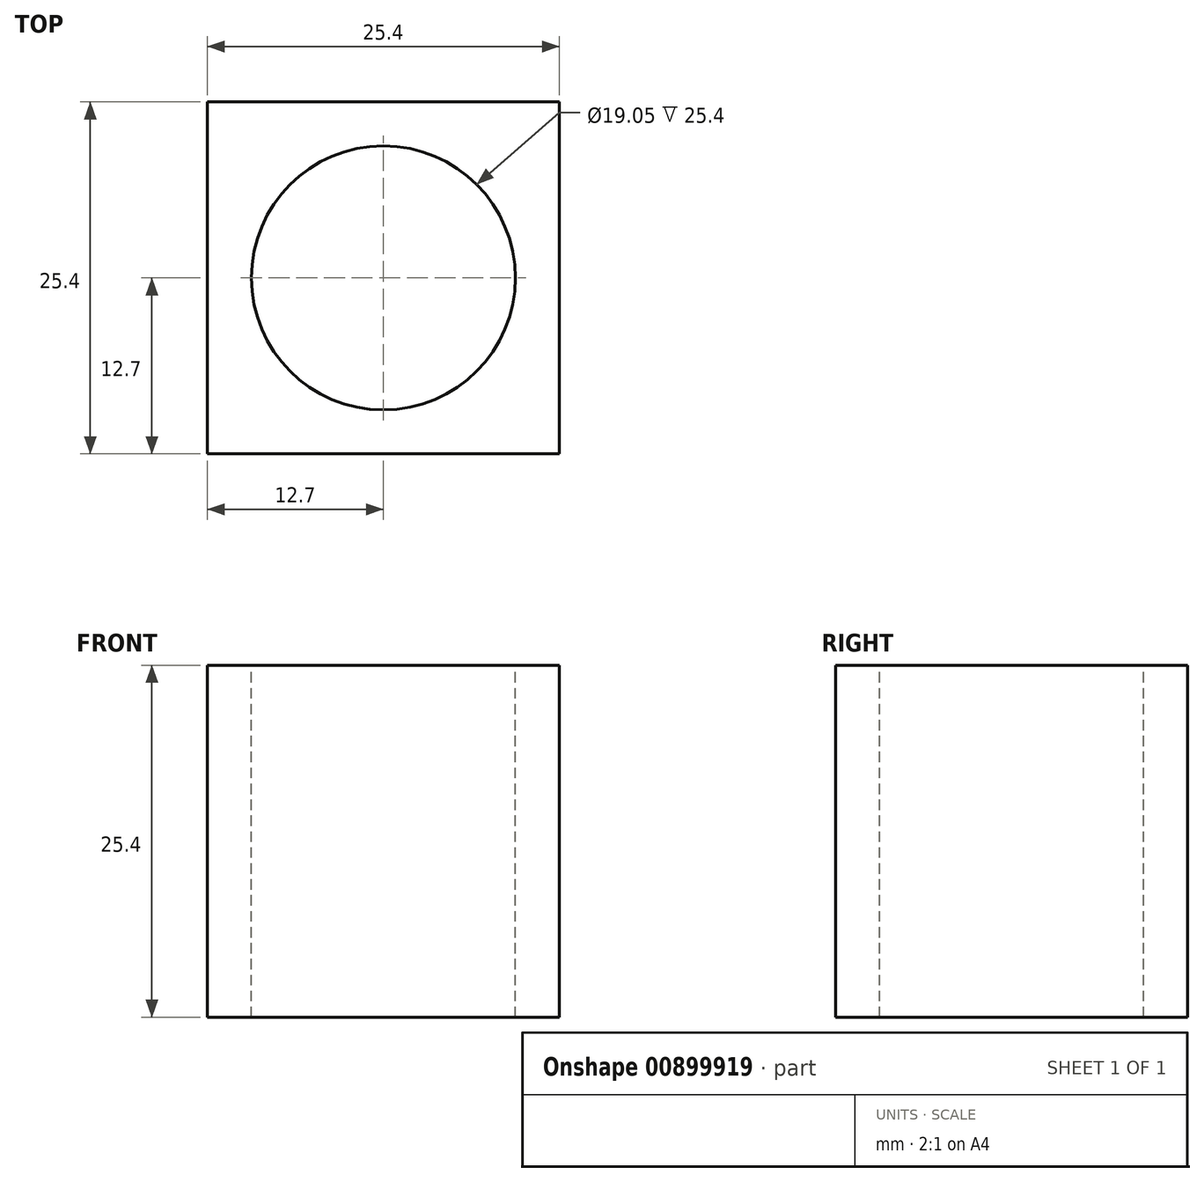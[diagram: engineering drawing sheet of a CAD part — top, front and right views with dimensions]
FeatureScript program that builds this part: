
annotation { "Feature Type Name" : "Feature", "Feature Type Description" : "" }
export const myFeature = defineFeature(function(context is Context, id is Id, definition is map)
    precondition{}
    {
        {
            var Q0;
            Q0=qCreatedBy(makeId("Top.planeOp"),FACE);
            var sketch = newSketch(context, id + "F0", { "sketchPlane" : qUnion([Q0])});
            skLineSegment(sketch, "E0.bottom", {"start": v(12.7, -12.7) * mm, "end": v(-12.7, -12.7) * mm});
            skLineSegment(sketch, "E0.top", {"start": v(12.7, 12.7) * mm, "end": v(-12.7, 12.7) * mm});
            skLineSegment(sketch, "E0.left", {"start": v(12.7, -12.7) * mm, "end": v(12.7, 12.7) * mm});
            skLineSegment(sketch, "E0.right", {"start": v(-12.7, -12.7) * mm, "end": v(-12.7, 12.7) * mm});
            skPoint(sketch, "E0.middle", {"position": v(0, 0) * mm});
            skSolve(sketch);
        }
        {
            var Q0;
            Q0=qSketchRegion(id+"F0",true);
            extrude(context, id + "F1", {"entities" : qUnion([Q0]), "depth" : 25.4 * mm, "offsetDistance" : 25.4 * mm});
        }
        {
            var Q0;
            Q0=makeQuery(id+"F1.opExtrude","CAP_FACE",FACE,{"disambiguationData":[OSD([sQuery(id+"F0.wireOp",EDGE,"E0.bottom"),sQuery(id+"F0.wireOp",EDGE,"E0.top"),sQuery(id+"F0.wireOp",EDGE,"E0.left"),sQuery(id+"F0.wireOp",EDGE,"E0.right")])],"isStart":false});
            var sketch = newSketch(context, id + "F2", { "sketchPlane" : qUnion([Q0])});
            skCircle(sketch, "E1", {"center": v(0, 0) * mm, "radius": 9.53 * mm});
            skSolve(sketch);
        }
        {
            var Q0;
            Q0=qSketchRegion(id+"F2",true);
            extrude(context, id + "F3", {"entities" : qUnion([Q0]), "operationType" : NewBodyOperationType.REMOVE, "endBound" : BoundingType.THROUGH_ALL, "oppositeDirection" : true, "depth" : 25.4 * mm, "offsetDistance" : 25.4 * mm});
        }
    });
